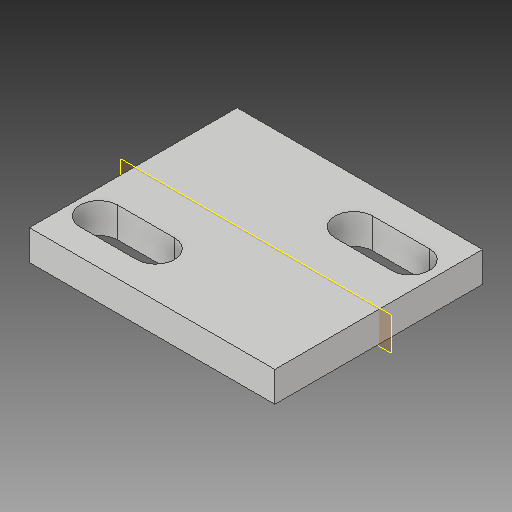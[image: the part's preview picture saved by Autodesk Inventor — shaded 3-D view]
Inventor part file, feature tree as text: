
AUTODESK INVENTOR PART (.ipt)
format: ipt  version: 2017 (Build 210142000, 142)  size: 114,176 bytes
history: native  units: mm
features: extrude x1, plane x1, sketch x1
ambient origin geometry x8: Origin, YZ Plane, XZ Plane, XY Plane, X Axis, Y Axis, Z Axis, Center Point
bodies: Solid1 (feature_tree)
feature tree (3):
  extrude  "Extrusion1"  Depth=22.0mm
  plane  "Work Plane1"
  sketch  "Sketch1"  dims[d0=26.0mm d1=22.0mm d5=6.0mm d6=4.0mm d9=3.2mm d10=0.0mm d12=6.0mm d13=4.0mm d14=12.5mm d15=14.5mm]
